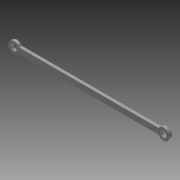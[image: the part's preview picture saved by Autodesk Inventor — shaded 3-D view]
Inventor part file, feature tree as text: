
AUTODESK INVENTOR PART (.ipt)
format: ipt  version: 2011 (Build 150239000, 239)  size: 93,184 bytes
history: native  units: in
note: dims shown in document units (in); Inventor stores cm internally (conversion verified against a paired STEP export)
features: extrude x3, sketch x3
ambient origin geometry x8: Origin, YZ Plane, XZ Plane, XY Plane, X Axis, Y Axis, Z Axis, Center Point
bodies: Solid1 (feature_tree)
feature tree (6):
  extrude  "Extrusion1"  Depth=0.25in
  extrude  "Extrusion2"  Depth=0.5in
  extrude  "Extrusion3"  Depth=0.125in TaperAngle=0.0deg
  sketch  "Sketch1"  dims[d0=6.5in d1=0.25in]
  sketch  "Sketch2"  dims[d2=0.125in d3=0.0in d4=0.5in]
  sketch  "Sketch3"  dims[d5=0.5in d6=0.125in d7=0.0in d8=0.5in d9=0.5in d10=0.125in d11=0.0in]
